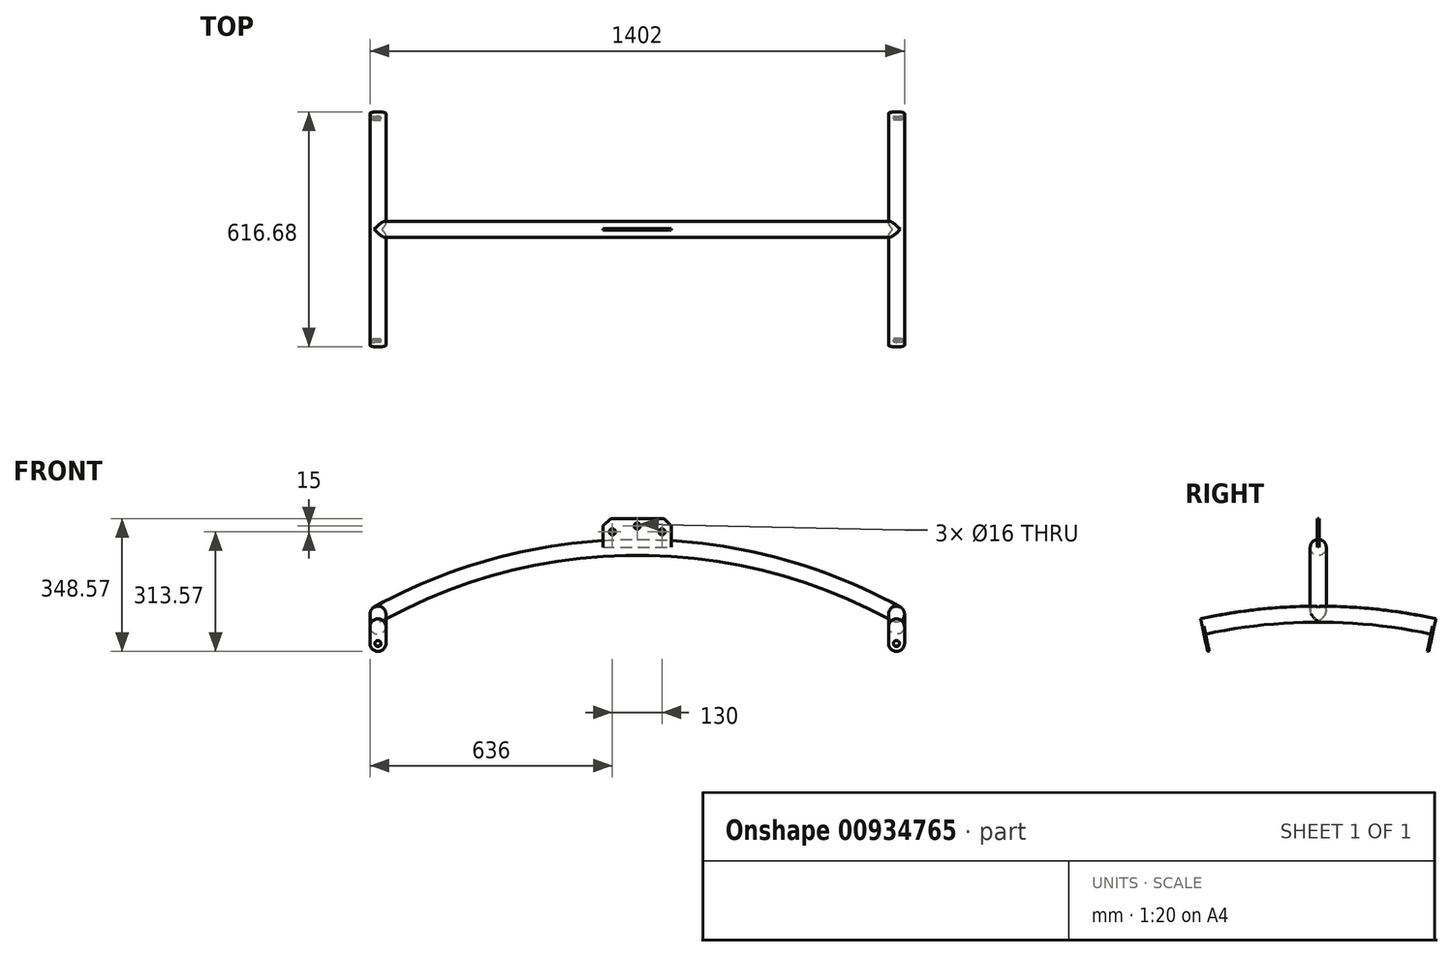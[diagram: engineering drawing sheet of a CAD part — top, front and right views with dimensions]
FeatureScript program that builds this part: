
annotation { "Feature Type Name" : "Feature", "Feature Type Description" : "" }
export const myFeature = defineFeature(function(context is Context, id is Id, definition is map)
    precondition{}
    {
        {
            var Q0;
            Q0=qCreatedBy(makeId("Front.planeOp"),FACE);
            var sketch = newSketch(context, id + "F0", { "sketchPlane" : qUnion([Q0])});
            skLineSegment(sketch, "E0", {"start": v(-143.12, 0) * mm, "end": v(139.16, 0) * mm, "construction": true});
            skPoint(sketch, "E1", {"position": v(-680, 0) * mm});
            skPoint(sketch, "E2", {"position": v(680, 0) * mm});
            skArc(sketch, "E3", {"start": v(680, 0) * mm, "mid": v(0, 175) * mm, "end": v(-680, 0) * mm});
            skPoint(sketch, "E4", {"position": v(0, 175) * mm});
            skCircle(sketch, "E5", {"center": v(-680, 0) * mm, "radius": 21 * mm});
            skLineSegment(sketch, "E6", {"start": v(0, 0) * mm, "end": v(0, 263.86) * mm, "construction": true});
            skCircle(sketch, "E7.MirrorC", {"center": v(680, 0) * mm, "radius": 21 * mm});
            skSolve(sketch);
        }
        {
            var Q0;
            Q0=qCreatedBy(makeId("Right.planeOp"),FACE);
            var sketch = newSketch(context, id + "F1", { "sketchPlane" : qUnion([Q0])});
            skPoint(sketch, "E8.0", {"position": v(0, 175) * mm});
            skCircle(sketch, "E9", {"center": v(0, 175) * mm, "radius": 21 * mm});
            skSolve(sketch);
        }
        {
            var Q0;
            Q0=makeQuery(id+"F1.imprint","IMPRINT",FACE,{"disambiguationData":[TD([[makeQuery(id+"F1.imprint","IMPRINT",EDGE,{"derivedFrom":sQuery(id+"F1.wireOp",EDGE,"E9")}),1.0]])]});
            var Q1;
            Q1=sQuery(id+"F0.wireOp",EDGE,"E3");
            sweep(context, id + "F2", {"profiles" : qUnion([Q0]), "path" : qUnion([Q1])});
        }
        {
            var Q0;
            Q0=sQuery(id+"F0.wireOp",VERTEX,"E1");
            var Q1;
            Q1=qCreatedBy(makeId("Right.planeOp"),FACE);
            cPlane(context, id + "F3", {"entities" : qUnion([Q0, Q1]), "cplaneType" : CPlaneType.PLANE_POINT, "offset" : 25 * mm, "width" : 150 * mm, "height" : 150 * mm});
        }
        {
            var Q0;
            Q0=qCreatedBy(id+"F3.planeOp",FACE);
            var sketch = newSketch(context, id + "F4", { "sketchPlane" : qUnion([Q0])});
            skLineSegment(sketch, "E10", {"start": v(0, 0) * mm, "end": v(0, -52.86) * mm, "construction": true});
            skLineSegment(sketch, "E11", {"start": v(300, -32) * mm, "end": v(-300, -32) * mm, "construction": true});
            skArc(sketch, "E12", {"start": v(300, -32) * mm, "mid": v(0, 0) * mm, "end": v(-300, -32) * mm});
            skSolve(sketch);
        }
        {
            var Q0;
            Q0=makeQuery(id+"F0.imprint","IMPRINT",FACE,{"disambiguationData":[TD([[makeQuery(id+"F0.imprint","IMPRINT",EDGE,{"derivedFrom":sQuery(id+"F0.wireOp",EDGE,"E5")}),1.0]])]});
            var Q1;
            Q1=sQuery(id+"F4.wireOp",EDGE,"E12");
            sweep(context, id + "F5", {"profiles" : qUnion([Q0]), "path" : qUnion([Q1])});
        }
        {
            var Q0;
            Q0=makeQuery(id+"F5.opSweep","SWEPT_BODY",BODY,{"disambiguationData":[OSD([sQuery(id+"F0.wireOp",EDGE,"E5"),sQuery(id+"F4.wireOp",EDGE,"E12")])]});
            var Q1;
            Q1=qCreatedBy(makeId("Right.planeOp"),FACE);
            mirror(context, id + "F6", {"entities" : qUnion([Q0]), "mirrorPlane" : qUnion([Q1])});
        }
        {
            var Q0;
            Q0=qCreatedBy(makeId("Top.planeOp"),FACE);
            var Q1;
            Q1=sQuery(id+"F0.wireOp",VERTEX,"E4");
            cPlane(context, id + "F7", {"entities" : qUnion([Q0, Q1]), "cplaneType" : CPlaneType.PLANE_POINT, "offset" : 25 * mm, "width" : 150 * mm, "height" : 150 * mm});
        }
        {
            var Q0;
            Q0=qCreatedBy(id+"F7.planeOp",FACE);
            var sketch = newSketch(context, id + "F8", { "sketchPlane" : qUnion([Q0])});
            skLineSegment(sketch, "E13.bottom", {"start": v(-90, -2) * mm, "end": v(90, -2) * mm});
            skLineSegment(sketch, "E13.top", {"start": v(-90, 2) * mm, "end": v(90, 2) * mm});
            skLineSegment(sketch, "E13.left", {"start": v(-90, -2) * mm, "end": v(-90, 2) * mm});
            skLineSegment(sketch, "E13.right", {"start": v(90, -2) * mm, "end": v(90, 2) * mm});
            skPoint(sketch, "E13.middle", {"position": v(0, 0) * mm});
            skSolve(sketch);
        }
        {
            var Q0;
            Q0 = qSketchRegion(id + "F8", true);
            extrude(context, id + "F9", {"entities" : qUnion([Q0]), "depth" : (55 + 42 / 2) * mm, "offsetDistance" : 25 * mm});
        }
        {
            var Q0;
            Q0=makeQuery(id+"F9.opExtrude","CAP_EDGE",EDGE,{"disambiguationData":[OSD([sQuery(id+"F8.wireOp",EDGE,"E13.right")])],"isStart":false});
            var Q1;
            Q1=makeQuery(id+"F9.opExtrude","CAP_EDGE",EDGE,{"disambiguationData":[OSD([sQuery(id+"F8.wireOp",EDGE,"E13.left")])],"isStart":false});
            chamfer(context, id + "F10", {"entities" : qUnion([Q0, Q1]), "width" : 20 * mm, "tangentPropagation" : true});
        }
        {
            var Q0;
            Q0=makeQuery(id+"F9.opExtrude","SWEPT_FACE",FACE,{"disambiguationData":[OSD([sQuery(id+"F8.wireOp",EDGE,"E13.top")])]});
            var sketch = newSketch(context, id + "F11", { "sketchPlane" : qUnion([Q0])});
            skCircle(sketch, "E14", {"center": v(0, 231) * mm, "radius": 8 * mm});
            skCircle(sketch, "E15", {"center": v(-65, 216) * mm, "radius": 8 * mm});
            skCircle(sketch, "E16.MirrorC", {"center": v(65, 216) * mm, "radius": 8 * mm});
            skSolve(sketch);
        }
        {
            var Q0;
            Q0 = qSketchRegion(id + "F11", true);
            extrude(context, id + "F12", {"entities" : qUnion([Q0]), "operationType" : NewBodyOperationType.REMOVE, "oppositeDirection" : true, "depth" : 25 * mm, "offsetDistance" : 25 * mm});
        }
        {
            var Q0;
            Q0=makeQuery(id+"F6.opPattern","COPY",FACE,{"derivedFrom":makeQuery(id+"F5.opSweep","CAP_FACE",FACE,{"disambiguationData":[OSD([sQuery(id+"F0.wireOp",EDGE,"E5"),sQuery(id+"F4.wireOp",VERTEX,"E12.start")])],"isStart":true}),"instanceName":"1"});
            var sketch = newSketch(context, id + "F13", { "sketchPlane" : qUnion([Q0])});
            skArc(sketch, "E17.0", {"start": v(-659, 32) * mm, "mid": v(-680, 53) * mm, "end": v(-701, 32) * mm});
            skLineSegment(sketch, "E18", {"start": v(-701, 32) * mm, "end": v(-701, -13.22) * mm});
            skLineSegment(sketch, "E19", {"start": v(-659, 32) * mm, "end": v(-659, -94.56) * mm});
            skLineSegment(sketch, "E20", {"start": v(-659, -13.22) * mm, "end": v(-659, 32) * mm});
            skArc(sketch, "E21", {"start": v(-701, -13.22) * mm, "mid": v(-680, -34.22) * mm, "end": v(-659, -13.22) * mm});
            skCircle(sketch, "E22", {"center": v(-680, -13.22) * mm, "radius": 8 * mm});
            skSolve(sketch);
        }
        {
            var Q0;
            Q0 = qSketchRegion(id + "F13", true);
            extrude(context, id + "F14", {"entities" : qUnion([Q0]), "depth" : 4 * mm, "offsetDistance" : 25 * mm});
        }
        {
            var Q0;
            Q0=makeQuery(id+"F14.opExtrude","SWEPT_BODY",BODY,{"disambiguationData":[OSD([sQuery(id+"F13.wireOp",EDGE,"E17.0"),sQuery(id+"F13.wireOp",EDGE,"E18"),sQuery(id+"F13.wireOp",EDGE,"E20"),sQuery(id+"F13.wireOp",EDGE,"E21"),sQuery(id+"F13.wireOp",EDGE,"E22")])]});
            var Q1;
            Q1=qCreatedBy(makeId("Front.planeOp"),FACE);
            mirror(context, id + "F15", {"operationType" : NewBodyOperationType.ADD, "entities" : qUnion([Q0]), "mirrorPlane" : qUnion([Q1])});
        }
        {
            var Q0;
            Q0=makeQuery(id+"F6.opPattern","COPY",BODY,{"derivedFrom":makeQuery(id+"F5.opSweep","SWEPT_BODY",BODY,{"disambiguationData":[OSD([sQuery(id+"F0.wireOp",EDGE,"E5"),sQuery(id+"F4.wireOp",EDGE,"E12")])]}),"instanceName":"1"});
            var Q1;
            Q1=qCreatedBy(makeId("Right.planeOp"),FACE);
            mirror(context, id + "F16", {"operationType" : NewBodyOperationType.ADD, "entities" : qUnion([Q0]), "mirrorPlane" : qUnion([Q1])});
        }
    });
